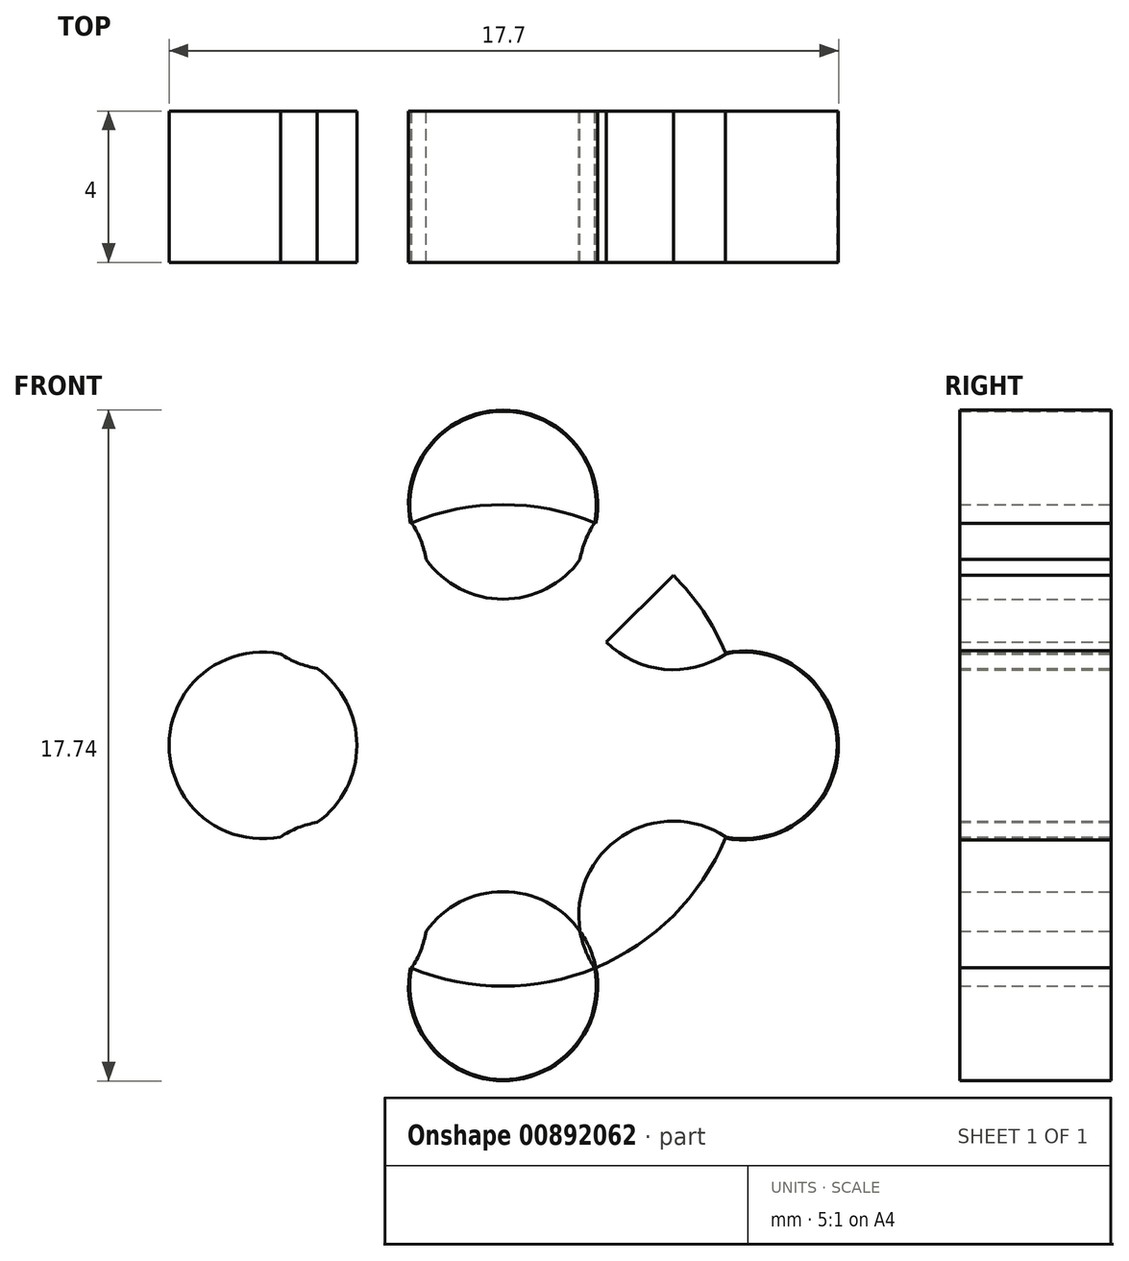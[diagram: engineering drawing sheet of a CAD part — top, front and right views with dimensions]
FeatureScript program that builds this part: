
annotation { "Feature Type Name" : "Feature", "Feature Type Description" : "" }
export const myFeature = defineFeature(function(context is Context, id is Id, definition is map)
    precondition{}
    {
        {
            var Q0;
            Q0=qCreatedBy(makeId("Front.planeOp"),FACE);
            var sketch = newSketch(context, id + "F0", { "sketchPlane" : qUnion([Q0])});
            skCircle(sketch, "E0", {"center": v(0, 0) * mm, "radius": 6.37 * mm});
            skCircle(sketch, "E1", {"center": v(0, 6.37) * mm, "radius": 2.5 * mm});
            skCircle(sketch, "E2.1.0", {"center": v(6.37, 0) * mm, "radius": 2.5 * mm});
            skCircle(sketch, "E2.2.0", {"center": v(0, -6.37) * mm, "radius": 2.5 * mm});
            skLineSegment(sketch, "E2.anchor1", {"start": v(0, 0) * mm, "end": v(0, 6.37) * mm, "construction": true});
            skLineSegment(sketch, "E2.anchor2", {"start": v(0, 0) * mm, "end": v(0, -6.37) * mm, "construction": true});
            skCircle(sketch, "E3.1.0", {"center": v(-6.37, 0) * mm, "radius": 2.5 * mm});
            skLineSegment(sketch, "E4", {"start": v(0, 0) * mm, "end": v(8.72, 8.72) * mm});
            skArc(sketch, "E5", {"start": v(2.42, 5.89) * mm, "mid": v(2.73, 2.73) * mm, "end": v(5.89, 2.42) * mm});
            skArc(sketch, "E6.1.0", {"start": v(5.89, -2.42) * mm, "mid": v(2.73, -2.73) * mm, "end": v(2.42, -5.89) * mm});
            skArc(sketch, "E6.2.0", {"start": v(-2.42, -5.89) * mm, "mid": v(-2.73, -2.73) * mm, "end": v(-5.89, -2.42) * mm});
            skLineSegment(sketch, "E6.anchor1", {"start": v(0, 0) * mm, "end": v(5.89, 2.42) * mm, "construction": true});
            skLineSegment(sketch, "E6.anchor2", {"start": v(0, 0) * mm, "end": v(-5.89, -2.42) * mm, "construction": true});
            skArc(sketch, "E7.1.0", {"start": v(-5.89, 2.42) * mm, "mid": v(-2.73, 2.73) * mm, "end": v(-2.42, 5.89) * mm});
            skLineSegment(sketch, "E7.anchor1", {"start": v(0, 0) * mm, "end": v(-4.5, -4.5) * mm, "construction": true});
            skLineSegment(sketch, "E7.anchor2", {"start": v(0, 0) * mm, "end": v(4.5, 4.5) * mm, "construction": true});
            skArc(sketch, "E8", {"start": v(-2.42, 5.89) * mm, "mid": v(0, 8.83) * mm, "end": v(2.42, 5.89) * mm});
            skArc(sketch, "E9", {"start": v(5.89, 2.42) * mm, "mid": v(8.83, 0) * mm, "end": v(5.89, -2.42) * mm});
            skArc(sketch, "E10", {"start": v(2.42, -5.89) * mm, "mid": v(0, -8.83) * mm, "end": v(-2.42, -5.89) * mm});
            skArc(sketch, "E11", {"start": v(-5.89, 2.42) * mm, "mid": v(-8.83, 0) * mm, "end": v(-5.89, -2.42) * mm});
            skSolve(sketch);
        }
        {
            var Q0;
            {var subQ0=sQuery(id+"F0.wireOp",EDGE,"E11");Q0=makeQuery(id+"F0.imprint","IMPRINT",FACE,{"disambiguationData":[TD([[makeQuery(id+"F0.imprint","IMPRINT",EDGE,{"derivedFrom":subQ0}),1.0]])]});}
            var Q1;
            {var subQ1=sQuery(id+"F0.wireOp",EDGE,"E6.2.0");var subQ6=sQuery(id+"F0.wireOp",EDGE,"E3.1.0");var subQ7=makeQuery(id+"F0.imprint","INTERSECT",VERTEX,{"derivedFrom":[subQ6,subQ1]});Q1=makeQuery(id+"F0.imprint","IMPRINT",FACE,{"disambiguationData":[TD([[makeQuery(id+"F0.imprint","IMPRINT",EDGE,{"disambiguationData":[TD([[subQ7,-1.0]])],"derivedFrom":subQ6}),1.0]])]});}
            var Q2;
            {var subQ3=sQuery(id+"F0.wireOp",EDGE,"E5");var subQ14=sQuery(id+"F0.wireOp",EDGE,"E2.1.0");var subQ15=makeQuery(id+"F0.imprint","INTERSECT",VERTEX,{"derivedFrom":[subQ14,subQ3]});Q2=makeQuery(id+"F0.imprint","IMPRINT",FACE,{"disambiguationData":[TD([[makeQuery(id+"F0.imprint","IMPRINT",EDGE,{"disambiguationData":[TD([[subQ15,-1.0]])],"derivedFrom":subQ14}),-1.0]])]});}
            var Q3;
            {var subQ1=sQuery(id+"F0.wireOp",EDGE,"E7.1.0");var subQ6=sQuery(id+"F0.wireOp",EDGE,"E1");var subQ7=makeQuery(id+"F0.imprint","INTERSECT",VERTEX,{"derivedFrom":[subQ6,subQ1]});Q3=makeQuery(id+"F0.imprint","IMPRINT",FACE,{"disambiguationData":[TD([[makeQuery(id+"F0.imprint","IMPRINT",EDGE,{"disambiguationData":[TD([[subQ7,-1.0]])],"derivedFrom":subQ6}),1.0]])]});}
            var Q4;
            {var subQ0=sQuery(id+"F0.wireOp",EDGE,"E8");Q4=makeQuery(id+"F0.imprint","IMPRINT",FACE,{"disambiguationData":[TD([[makeQuery(id+"F0.imprint","IMPRINT",EDGE,{"derivedFrom":subQ0}),-1.0]])]});}
            var Q5;
            {var subQ4=sQuery(id+"F0.wireOp",EDGE,"E5");var subQ6=sQuery(id+"F0.wireOp",EDGE,"E2.1.0");var subQ7=makeQuery(id+"F0.imprint","INTERSECT",VERTEX,{"derivedFrom":[subQ6,subQ4]});Q5=makeQuery(id+"F0.imprint","IMPRINT",FACE,{"disambiguationData":[TD([[makeQuery(id+"F0.imprint","IMPRINT",EDGE,{"disambiguationData":[TD([[subQ7,-1.0]])],"derivedFrom":subQ6}),1.0]])]});}
            var Q6;
            {var subQ0=sQuery(id+"F0.wireOp",EDGE,"E9");Q6=makeQuery(id+"F0.imprint","IMPRINT",FACE,{"disambiguationData":[TD([[makeQuery(id+"F0.imprint","IMPRINT",EDGE,{"derivedFrom":subQ0}),-1.0]])]});}
            var Q7;
            {var subQ1=sQuery(id+"F0.wireOp",EDGE,"E6.1.0");var subQ6=sQuery(id+"F0.wireOp",EDGE,"E2.2.0");var subQ7=makeQuery(id+"F0.imprint","INTERSECT",VERTEX,{"derivedFrom":[subQ6,subQ1]});Q7=makeQuery(id+"F0.imprint","IMPRINT",FACE,{"disambiguationData":[TD([[makeQuery(id+"F0.imprint","IMPRINT",EDGE,{"disambiguationData":[TD([[subQ7,-1.0]])],"derivedFrom":subQ6}),1.0]])]});}
            var Q8;
            {var subQ0=sQuery(id+"F0.wireOp",EDGE,"E10");Q8=makeQuery(id+"F0.imprint","IMPRINT",FACE,{"disambiguationData":[TD([[makeQuery(id+"F0.imprint","IMPRINT",EDGE,{"derivedFrom":subQ0}),-1.0]])]});}
            extrude(context, id + "F1", {"entities" : qUnion([Q0, Q1, Q2, Q3, Q4, Q5, Q6, Q7, Q8]), "depth" : 4 * mm, "offsetDistance" : 25 * mm});
        }
        {
            var Q0;
            Q0=sQuery(id+"F0.wireOp",VERTEX,"E0.center");
            var Q1;
            Q1=makeQuery(id+"F1.opExtrude","SWEPT_BODY",BODY,{"disambiguationData":[OSD([sQuery(id+"F0.wireOp",EDGE,"E6.1.0"),sQuery(id+"F0.wireOp",EDGE,"E6.2.0"),sQuery(id+"F0.wireOp",EDGE,"E7.1.0"),sQuery(id+"F0.wireOp",EDGE,"E5"),sQuery(id+"F0.wireOp",EDGE,"E8"),sQuery(id+"F0.wireOp",EDGE,"E9"),sQuery(id+"F0.wireOp",EDGE,"E10"),sQuery(id+"F0.wireOp",EDGE,"E11")])]});
            hole(context, id + "F2", {"style" : HoleStyle.SIMPLE, "endStyle" : HoleEndStyle.THROUGH, "oppositeDirection" : true, "holeDiameter" : 3.5 * mm, "majorDiameter" : 5 * mm, "isTappedThrough" : true, "tappedDepth" : 12 * mm, "tapClearance" : 3, "locations" : qUnion([Q0]), "scope" : qUnion([Q1])});
        }
    });
